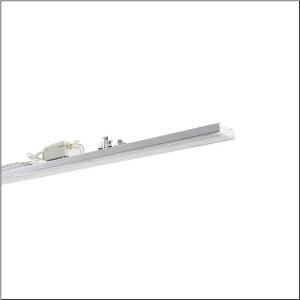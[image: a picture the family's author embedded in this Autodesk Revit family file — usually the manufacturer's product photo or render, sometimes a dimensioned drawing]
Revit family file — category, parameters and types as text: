
# Revit family: licross_r__21_recessed_mo_52tl14dv4exg_de02
name_source: partatom
category: Lighting Fixtures
units: mm (PartAtom-declared; Revit-internal decimal feet)

## family parameters
Cut with Voids When Loaded = No
Host = Face
Light Source = No
Part Type = Normal
Room Calculation Point = No
Round Connector Dimension = Use Diameter
Shared = No

## types (1)
- --- (1 x LED, 14200 lm, 85.3 W, 4000K)
    Apparent Load = 85 VA
    CIE Flux Codes = 56 84 97 100 100
    Color Rendering = 80
    Color Temperature = 4000K
    Default Elevation = 1800 mm
    Description = Licross® 21 Recessed MO, luminaire insert, of sheet steel, galvanised, coil coated, white, length: 2.250mm, width: 66mm, height: 67mm, LED rated luminous flux: 14.200lm, light colour: 840, control gear: DALI 2, with plug, 5-pole, with phase selection, mains connection: 220..240V, AC, 50/60Hz, rated input power: 85W, halogen-free wiring, primary light control with lens, of plastic, primary optical cover: cover, of PMMA, light emission: direct distribution, primary light characteristic: asymmetric, protection rating (complete): IP40, insulation class (complete): insulation class I (protective earthing), certification: CE, ENEC, VDE, UKCA, protection symbol: D if used in an environment without relevant dust loads with corresponding accessories, impact resistance: IK06, permissible ambient temperature for indoor applications: -25..+35°C, corresponds to IFS (International Featured Standards) requirements for safety and quality in the food industry, reducing of maximum allowable ambient temperature of 5°C with ceiling mounting, LABS conformity tested according to VDMA 24364:2018-05, packaging unit: 1 piece
    Height = 58 mm
    Lamp = 1 x LED
    Lamp Light Flux = 14200 lm
    Lamp Power = 85.3 W
    Lamp count = 1
    Length = 2250 mm
    Luminous efficacy = 166 lm/W
    Manufacturer = Siteco
    ModVariant = No
    Model = 52TL14DV4EXG
    Mounting Place = Ceiling
    Mounting Type = Pendant
    Number of Poles = 1
    OnlyDefault = Yes
    Power Factor = 1
    Product Name = Licross® 21 Recessed MO
    Product group = luminaire insert
    ProductGroupID = 901
    Protection Class = Protection class I
    Protection Degree = IP 40
    RLX_Detail_Level = 1
    RLX_Emergency_Light_Flux = 0 lm
    RLX_Emergency_Type = 0
    RLX_Emergency_Type_DB = No
    RlxData = <blob elided: 29721 chars, md5=383af9d9>
    Socket = socket
    Standby Power = 0 W
    System Light Flux = 14200 lm
    System Power = 85 W
    Type Comments = factory setting: luminous flux: 100 % | dim-lin: 254 | 390 mA
    Type Image = l_1296930.jpg
    URL = http://relux.com
    VarID = @adj_059453
    Voltage = 0 V
    Weight = 0.00 kg
    Width = 66 mm

## geometry (parser evidence)
native form markers: Blend x4, Sweep x9
no freeform markers — native parametric forms only
